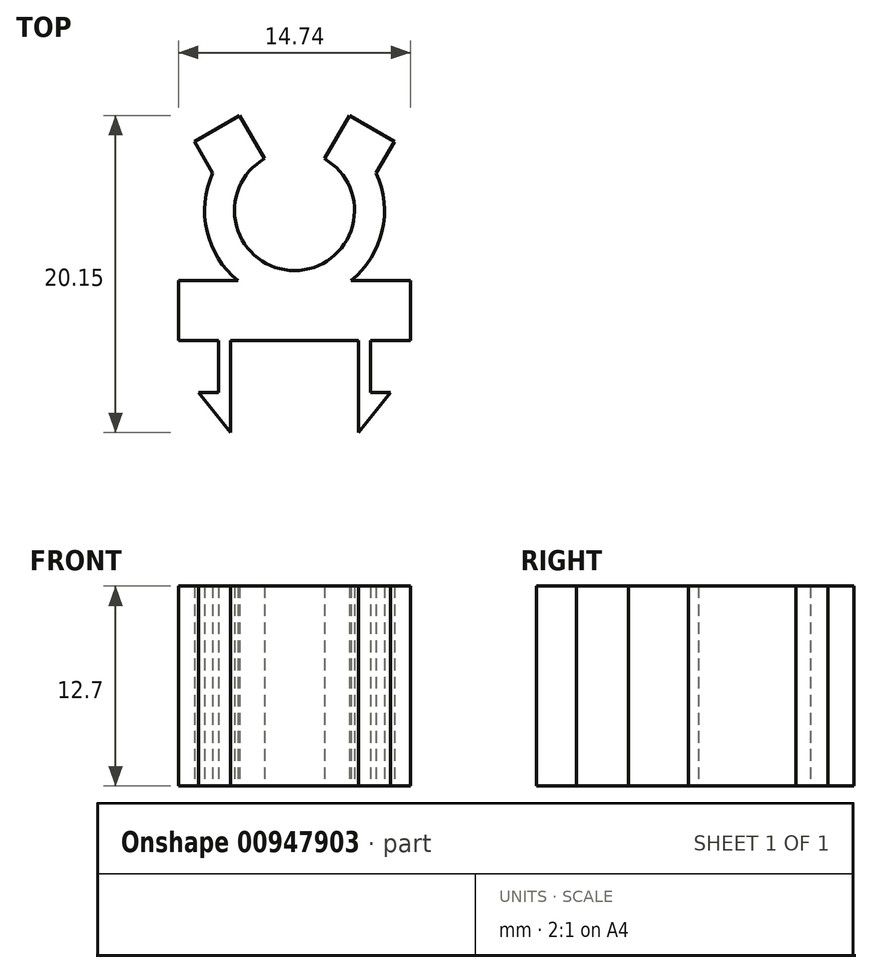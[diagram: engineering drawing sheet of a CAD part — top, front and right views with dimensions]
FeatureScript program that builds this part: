
annotation { "Feature Type Name" : "Feature", "Feature Type Description" : "" }
export const myFeature = defineFeature(function(context is Context, id is Id, definition is map)
    precondition{}
    {
        {
            var Q0;
            Q0=qCreatedBy(makeId("Top.planeOp"),FACE);
            var sketch = newSketch(context, id + "F0", { "sketchPlane" : qUnion([Q0])});
            skArc(sketch, "E0", {"start": v(-1.9, 3.3) * mm, "mid": v(0, -3.81) * mm, "end": v(1.9, 3.3) * mm});
            skArc(sketch, "E1", {"start": v(-5.2, 2.4) * mm, "mid": v(-5.56, -1.3) * mm, "end": v(-3.59, -4.45) * mm});
            skLineSegment(sketch, "E2", {"start": v(1.9, 3.3) * mm, "end": v(3.5, 6.05) * mm});
            skLineSegment(sketch, "E3", {"start": v(-1.9, 3.3) * mm, "end": v(-3.5, 6.05) * mm});
            skLineSegment(sketch, "E4", {"start": v(-3.5, 6.05) * mm, "end": v(-6.35, 4.4) * mm});
            skLineSegment(sketch, "E5", {"start": v(-6.35, 4.4) * mm, "end": v(-3.81, 0) * mm});
            skLineSegment(sketch, "E6", {"start": v(3.5, 6.05) * mm, "end": v(6.35, 4.4) * mm});
            skLineSegment(sketch, "E7", {"start": v(6.35, 4.4) * mm, "end": v(3.8, 0) * mm});
            skLineSegment(sketch, "E8", {"start": v(7.37, -4.45) * mm, "end": v(3.59, -4.45) * mm});
            skLineSegment(sketch, "E9", {"start": v(-7.37, -4.45) * mm, "end": v(-7.37, -8.26) * mm});
            skLineSegment(sketch, "E10", {"start": v(-7.37, -8.26) * mm, "end": v(-4.83, -8.26) * mm});
            skLineSegment(sketch, "E11", {"start": v(-4.83, -8.26) * mm, "end": v(-4.83, -11.56) * mm});
            skLineSegment(sketch, "E12", {"start": v(-4.83, -11.56) * mm, "end": v(-6.1, -11.56) * mm});
            skLineSegment(sketch, "E13", {"start": v(-4.06, -14.1) * mm, "end": v(-4.06, -8.26) * mm});
            skLineSegment(sketch, "E14.MirrorCS", {"start": v(4.06, -14.1) * mm, "end": v(4.06, -8.26) * mm});
            skLineSegment(sketch, "E15.MirrorCS", {"start": v(7.37, -8.26) * mm, "end": v(4.83, -8.26) * mm});
            skLineSegment(sketch, "E16.MirrorCS", {"start": v(4.83, -8.26) * mm, "end": v(4.83, -11.56) * mm});
            skLineSegment(sketch, "E17.MirrorCS", {"start": v(4.83, -11.56) * mm, "end": v(6.1, -11.56) * mm});
            skLineSegment(sketch, "E18.MirrorCS", {"start": v(7.37, -4.45) * mm, "end": v(7.37, -8.26) * mm});
            skLineSegment(sketch, "E19", {"start": v(-4.06, -8.26) * mm, "end": v(4.06, -8.26) * mm});
            skLineSegment(sketch, "E20.MirrorCS", {"start": v(4.06, -8.26) * mm, "end": v(-4.06, -8.26) * mm});
            skLineSegment(sketch, "E21.trimOffspring", {"start": v(-3.59, -4.45) * mm, "end": v(-7.37, -4.45) * mm});
            skArc(sketch, "E22.trimOffspring", {"start": v(3.59, -4.45) * mm, "mid": v(5.56, -1.3) * mm, "end": v(5.2, 2.4) * mm});
            skLineSegment(sketch, "E23", {"start": v(-6.1, -11.56) * mm, "end": v(-4.06, -14.1) * mm});
            skLineSegment(sketch, "E24", {"start": v(6.1, -11.56) * mm, "end": v(4.06, -14.1) * mm});
            skSolve(sketch);
        }
        {
            var Q0;
            {var subQ6=sQuery(id+"F0.wireOp",EDGE,"E1");Q0=makeQuery(id+"F0.imprint","IMPRINT",FACE,{"disambiguationData":[TD([[makeQuery(id+"F0.imprint","IMPRINT",EDGE,{"derivedFrom":subQ6}),1.0]])]});}
            var Q1;
            {var subQ3=sQuery(id+"F0.wireOp",EDGE,"E2");Q1=makeQuery(id+"F0.imprint","IMPRINT",FACE,{"disambiguationData":[TD([[makeQuery(id+"F0.imprint","IMPRINT",EDGE,{"derivedFrom":subQ3}),-1.0]])]});}
            var Q2;
            {var subQ3=sQuery(id+"F0.wireOp",EDGE,"E3");Q2=makeQuery(id+"F0.imprint","IMPRINT",FACE,{"disambiguationData":[TD([[makeQuery(id+"F0.imprint","IMPRINT",EDGE,{"derivedFrom":subQ3}),1.0]])]});}
            extrude(context, id + "F1", {"entities" : qUnion([Q0, Q1, Q2]), "depth" : 12.7 * mm, "offsetDistance" : 25.4 * mm});
        }
    });
